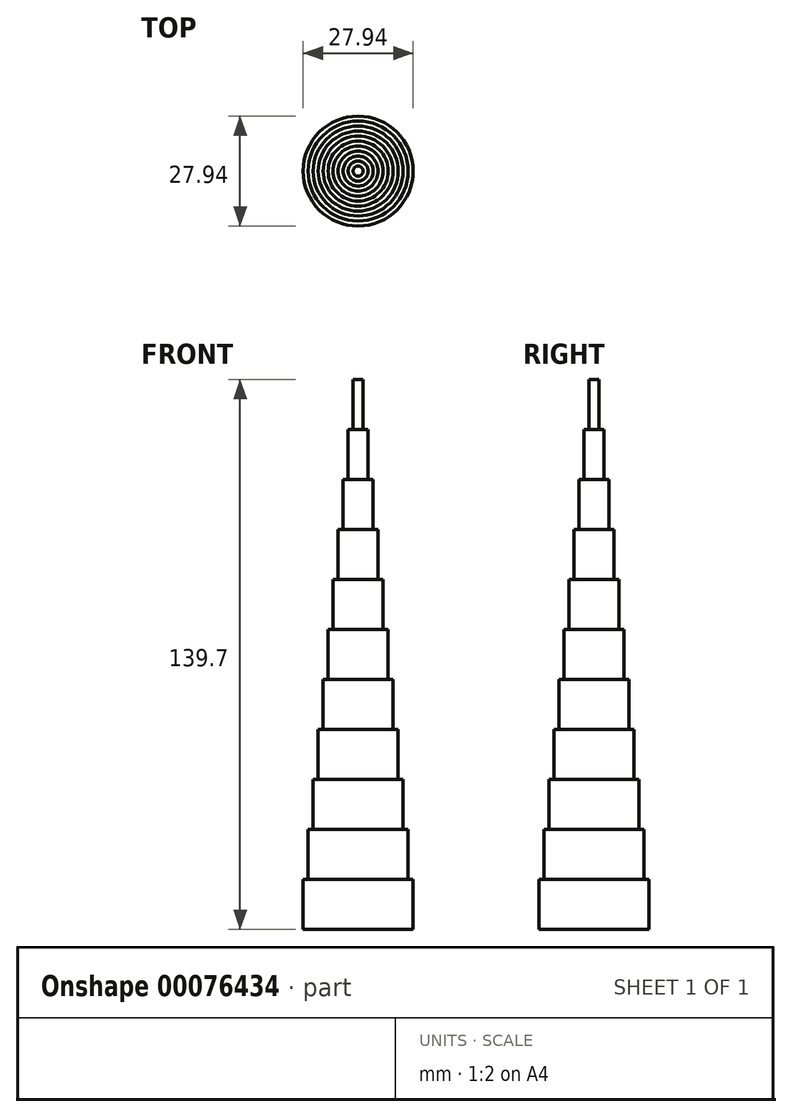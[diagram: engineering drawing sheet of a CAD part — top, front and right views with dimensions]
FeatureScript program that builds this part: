
annotation { "Feature Type Name" : "Feature", "Feature Type Description" : "" }
export const myFeature = defineFeature(function(context is Context, id is Id, definition is map)
    precondition{}
    {
        {
            var Q0;
            Q0=qCreatedBy(makeId("Top.planeOp"),FACE);
            var sketch = newSketch(context, id + "F0", { "sketchPlane" : qUnion([Q0])});
            skCircle(sketch, "E0", {"center": v(0, 0) * mm, "radius": 13.97 * mm});
            skSolve(sketch);
        }
        {
            var Q0;
            Q0=makeQuery(id+"F0.imprint","IMPRINT",FACE,{"disambiguationData":[TD([[makeQuery(id+"F0.imprint","IMPRINT",EDGE,{"derivedFrom":sQuery(id+"F0.wireOp",EDGE,"E0")}),1.0]])]});
            extrude(context, id + "F1", {"entities" : qUnion([Q0]), "depth" : 12.7 * mm});
        }
        {
            var Q0;
            Q0=makeQuery(id+"F1.opExtrude","CAP_FACE",FACE,{"disambiguationData":[OSD([sQuery(id+"F0.wireOp",EDGE,"E0")])],"isStart":false});
            var sketch = newSketch(context, id + "F2", { "sketchPlane" : qUnion([Q0])});
            skCircle(sketch, "E1", {"center": v(0, 0) * mm, "radius": 12.7 * mm});
            skSolve(sketch);
        }
        {
            var Q0;
            Q0=makeQuery(id+"F2.imprint","IMPRINT",FACE,{"disambiguationData":[TD([[makeQuery(id+"F2.imprint","IMPRINT",EDGE,{"derivedFrom":sQuery(id+"F2.wireOp",EDGE,"E1")}),1.0]])]});
            extrude(context, id + "F3", {"entities" : qUnion([Q0]), "operationType" : NewBodyOperationType.ADD, "depth" : 12.7 * mm});
        }
        {
            var Q0;
            Q0=makeQuery(id+"F3.opExtrude","CAP_FACE",FACE,{"disambiguationData":[OSD([sQuery(id+"F2.wireOp",EDGE,"E1")])],"isStart":false});
            var sketch = newSketch(context, id + "F4", { "sketchPlane" : qUnion([Q0])});
            skCircle(sketch, "E2", {"center": v(0, 0) * mm, "radius": 11.43 * mm});
            skSolve(sketch);
        }
        {
            var Q0;
            Q0=makeQuery(id+"F4.imprint","IMPRINT",FACE,{"disambiguationData":[TD([[makeQuery(id+"F4.imprint","IMPRINT",EDGE,{"derivedFrom":sQuery(id+"F4.wireOp",EDGE,"E2")}),1.0]])]});
            extrude(context, id + "F5", {"entities" : qUnion([Q0]), "operationType" : NewBodyOperationType.ADD, "depth" : 12.7 * mm});
        }
        {
            var Q0;
            Q0=makeQuery(id+"F5.opExtrude","CAP_FACE",FACE,{"disambiguationData":[OSD([sQuery(id+"F4.wireOp",EDGE,"E2")])],"isStart":false});
            var sketch = newSketch(context, id + "F6", { "sketchPlane" : qUnion([Q0])});
            skCircle(sketch, "E3", {"center": v(0, 0) * mm, "radius": 10.16 * mm});
            skSolve(sketch);
        }
        {
            var Q0;
            Q0=makeQuery(id+"F6.imprint","IMPRINT",FACE,{"disambiguationData":[TD([[makeQuery(id+"F6.imprint","IMPRINT",EDGE,{"derivedFrom":sQuery(id+"F6.wireOp",EDGE,"E3")}),1.0]])]});
            extrude(context, id + "F7", {"entities" : qUnion([Q0]), "operationType" : NewBodyOperationType.ADD, "depth" : 12.7 * mm});
        }
        {
            var Q0;
            Q0=makeQuery(id+"F7.opExtrude","CAP_FACE",FACE,{"disambiguationData":[OSD([sQuery(id+"F6.wireOp",EDGE,"E3")])],"isStart":false});
            var sketch = newSketch(context, id + "F8", { "sketchPlane" : qUnion([Q0])});
            skCircle(sketch, "E4", {"center": v(0, 0) * mm, "radius": 8.9 * mm});
            skSolve(sketch);
        }
        {
            var Q0;
            Q0=makeQuery(id+"F8.imprint","IMPRINT",FACE,{"disambiguationData":[TD([[makeQuery(id+"F8.imprint","IMPRINT",EDGE,{"derivedFrom":sQuery(id+"F8.wireOp",EDGE,"E4")}),1.0]])]});
            extrude(context, id + "F9", {"entities" : qUnion([Q0]), "operationType" : NewBodyOperationType.ADD, "depth" : 12.7 * mm});
        }
        {
            var Q0;
            Q0=makeQuery(id+"F9.opExtrude","CAP_FACE",FACE,{"disambiguationData":[OSD([sQuery(id+"F8.wireOp",EDGE,"E4")])],"isStart":false});
            var sketch = newSketch(context, id + "F10", { "sketchPlane" : qUnion([Q0])});
            skCircle(sketch, "E5", {"center": v(0, 0) * mm, "radius": 7.62 * mm});
            skSolve(sketch);
        }
        {
            var Q0;
            Q0=makeQuery(id+"F10.imprint","IMPRINT",FACE,{"disambiguationData":[TD([[makeQuery(id+"F10.imprint","IMPRINT",EDGE,{"derivedFrom":sQuery(id+"F10.wireOp",EDGE,"E5")}),1.0]])]});
            extrude(context, id + "F11", {"entities" : qUnion([Q0]), "operationType" : NewBodyOperationType.ADD, "depth" : 12.7 * mm});
        }
        {
            var Q0;
            Q0=makeQuery(id+"F11.opExtrude","CAP_FACE",FACE,{"disambiguationData":[OSD([sQuery(id+"F10.wireOp",EDGE,"E5")])],"isStart":false});
            var sketch = newSketch(context, id + "F12", { "sketchPlane" : qUnion([Q0])});
            skCircle(sketch, "E6", {"center": v(0, 0) * mm, "radius": 6.35 * mm});
            skSolve(sketch);
        }
        {
            var Q0;
            Q0=makeQuery(id+"F12.imprint","IMPRINT",FACE,{"disambiguationData":[TD([[makeQuery(id+"F12.imprint","IMPRINT",EDGE,{"derivedFrom":sQuery(id+"F12.wireOp",EDGE,"E6")}),1.0]])]});
            extrude(context, id + "F13", {"entities" : qUnion([Q0]), "operationType" : NewBodyOperationType.ADD, "depth" : 12.7 * mm});
        }
        {
            var Q0;
            Q0=makeQuery(id+"F13.opExtrude","CAP_FACE",FACE,{"disambiguationData":[OSD([sQuery(id+"F12.wireOp",EDGE,"E6")])],"isStart":false});
            var sketch = newSketch(context, id + "F14", { "sketchPlane" : qUnion([Q0])});
            skCircle(sketch, "E7", {"center": v(0, 0) * mm, "radius": 5.08 * mm});
            skSolve(sketch);
        }
        {
            var Q0;
            Q0=makeQuery(id+"F14.imprint","IMPRINT",FACE,{"disambiguationData":[TD([[makeQuery(id+"F14.imprint","IMPRINT",EDGE,{"derivedFrom":sQuery(id+"F14.wireOp",EDGE,"E7")}),1.0]])]});
            extrude(context, id + "F15", {"entities" : qUnion([Q0]), "operationType" : NewBodyOperationType.ADD, "depth" : 12.7 * mm});
        }
        {
            var Q0;
            Q0=makeQuery(id+"F15.opExtrude","CAP_FACE",FACE,{"disambiguationData":[OSD([sQuery(id+"F14.wireOp",EDGE,"E7")])],"isStart":false});
            var sketch = newSketch(context, id + "F16", { "sketchPlane" : qUnion([Q0])});
            skCircle(sketch, "E8", {"center": v(0, 0) * mm, "radius": 3.8 * mm});
            skSolve(sketch);
        }
        {
            var Q0;
            Q0=makeQuery(id+"F16.imprint","IMPRINT",FACE,{"disambiguationData":[TD([[makeQuery(id+"F16.imprint","IMPRINT",EDGE,{"derivedFrom":sQuery(id+"F16.wireOp",EDGE,"E8")}),1.0]])]});
            extrude(context, id + "F17", {"entities" : qUnion([Q0]), "operationType" : NewBodyOperationType.ADD, "depth" : 12.7 * mm});
        }
        {
            var Q0;
            Q0=makeQuery(id+"F17.opExtrude","CAP_FACE",FACE,{"disambiguationData":[OSD([sQuery(id+"F16.wireOp",EDGE,"E8")])],"isStart":false});
            var sketch = newSketch(context, id + "F18", { "sketchPlane" : qUnion([Q0])});
            skCircle(sketch, "E9", {"center": v(0, 0) * mm, "radius": 2.54 * mm});
            skSolve(sketch);
        }
        {
            var Q0;
            Q0=makeQuery(id+"F18.imprint","IMPRINT",FACE,{"disambiguationData":[TD([[makeQuery(id+"F18.imprint","IMPRINT",EDGE,{"derivedFrom":sQuery(id+"F18.wireOp",EDGE,"E9")}),1.0]])]});
            extrude(context, id + "F19", {"entities" : qUnion([Q0]), "operationType" : NewBodyOperationType.ADD, "depth" : 12.7 * mm});
        }
        {
            var Q0;
            Q0=makeQuery(id+"F19.opExtrude","CAP_FACE",FACE,{"disambiguationData":[OSD([sQuery(id+"F18.wireOp",EDGE,"E9")])],"isStart":false});
            var sketch = newSketch(context, id + "F20", { "sketchPlane" : qUnion([Q0])});
            skCircle(sketch, "E10", {"center": v(0, 0) * mm, "radius": 1.27 * mm});
            skSolve(sketch);
        }
        {
            var Q0;
            Q0=makeQuery(id+"F20.imprint","IMPRINT",FACE,{"disambiguationData":[TD([[makeQuery(id+"F20.imprint","IMPRINT",EDGE,{"derivedFrom":sQuery(id+"F20.wireOp",EDGE,"E10")}),1.0]])]});
            extrude(context, id + "F21", {"entities" : qUnion([Q0]), "operationType" : NewBodyOperationType.ADD, "depth" : 12.7 * mm});
        }
    });
